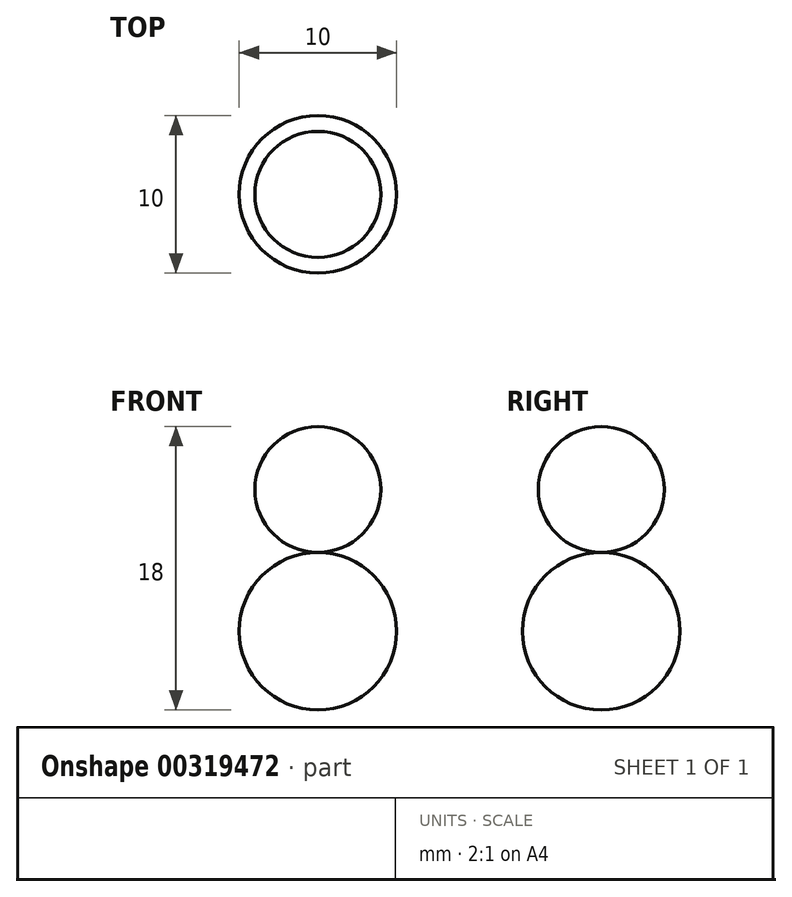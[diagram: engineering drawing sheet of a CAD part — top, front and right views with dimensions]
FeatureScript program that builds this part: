
annotation { "Feature Type Name" : "Feature", "Feature Type Description" : "" }
export const myFeature = defineFeature(function(context is Context, id is Id, definition is map)
    precondition{}
    {
        {
            var Q0;
            Q0=qCreatedBy(makeId("Front.planeOp"),FACE);
            var sketch = newSketch(context, id + "F0", { "sketchPlane" : qUnion([Q0])});
            skCircle(sketch, "E0", {"center": v(0, 0) * mm, "radius": 5 * mm});
            skCircle(sketch, "E1", {"center": v(0, 9) * mm, "radius": 4 * mm});
            skSolve(sketch);
        }
        {
            var Q0;
            Q0=makeQuery(id+"F0.imprint","IMPRINT",FACE,{"disambiguationData":[TD([[makeQuery(id+"F0.imprint","IMPRINT",EDGE,{"derivedFrom":sQuery(id+"F0.wireOp",EDGE,"E0")}),1.0]])]});
            extrude(context, id + "F1", {"entities" : qUnion([Q0]), "depth" : 5 * mm, "hasSecondDirection" : true, "secondDirectionOppositeDirection" : true, "secondDirectionDepth" : 5 * mm});
        }
        {
            var Q0;
            Q0=makeQuery(id+"F1.opExtrude","CAP_EDGE",EDGE,{"disambiguationData":[OSD([sQuery(id+"F0.wireOp",EDGE,"E0")])],"isStart":false});
            var Q1;
            Q1=makeQuery(id+"F1.opExtrude","CAP_EDGE",EDGE,{"disambiguationData":[OSD([sQuery(id+"F0.wireOp",EDGE,"E0")])],"isStart":true});
            fillet(context, id + "F2", {"entities" : qUnion([Q0, Q1]), "radius" : 5 * mm, "tangentPropagation" : true, "allowEdgeOverflow" : false});
        }
        {
            var Q0;
            Q0=makeQuery(id+"F0.imprint","IMPRINT",FACE,{"disambiguationData":[TD([[makeQuery(id+"F0.imprint","IMPRINT",EDGE,{"derivedFrom":sQuery(id+"F0.wireOp",EDGE,"E1")}),1.0]])]});
            extrude(context, id + "F3", {"entities" : qUnion([Q0]), "depth" : 4 * mm, "hasSecondDirection" : true, "secondDirectionOppositeDirection" : true, "secondDirectionDepth" : 4 * mm});
        }
        {
            var Q0;
            Q0=makeQuery(id+"F1.opExtrude","CAP_EDGE",EDGE,{"disambiguationData":[OSD([sQuery(id+"F0.wireOp",EDGE,"E1")])],"isStart":false});
            var Q1;
            Q1=makeQuery(id+"F1.opExtrude","CAP_EDGE",EDGE,{"disambiguationData":[OSD([sQuery(id+"F0.wireOp",EDGE,"E1")])],"isStart":true});
            var Q2;
            Q2=makeQuery(id+"F3.opExtrude","CAP_EDGE",EDGE,{"disambiguationData":[OSD([sQuery(id+"F0.wireOp",EDGE,"E1")])],"isStart":true});
            var Q3;
            Q3=makeQuery(id+"F3.opExtrude","CAP_EDGE",EDGE,{"disambiguationData":[OSD([sQuery(id+"F0.wireOp",EDGE,"E1")])],"isStart":false});
            fillet(context, id + "F4", {"entities" : qUnion([Q0, Q1, Q2, Q3]), "radius" : 4 * mm, "tangentPropagation" : true, "allowEdgeOverflow" : false});
        }
    });
